# Revit family: kitchen_Sinks_Sanindusa_Belfast_With-Popup-Waste
name_source: partatom
category: Plumbing Fixtures
revit_build: Autodesk Revit 2018 (Build: 20170223_1515(x64)
units: mm (PartAtom-declared; Revit-internal decimal feet)

## family parameters
Cut with Voids When Loaded = No
Host = Face
Part Type = Normal
Room Calculation Point = No
Round Connector Dimension = Use Diameter
Shared = No

## types (1)
- kitchen_Sinks_Sanindusa_Belfast_With-Popup-Waste
    AssetType = Fixed
    CodePerformance = EN 13310:2015
    Color = white
    Constituents = Pop up waste for kitchen sink ref.4740 (included); Siphon ref. 473000 (not included)
    Default Elevation = 1219 mm
    Description = 60x46 belfast kitchen sink with pop up waste
    DrainSize = 62 mm  [stored 0.203412 ft]
    Features = "Versatile installation: topmount or undermount. Glazed on all sides except on the basis of settlement
Not rectified"
    Finish = gloss
    Installation Instructions = https://www.tec.sanindusa.pt
    Manufacturer = Sanindusa
    ManufacturerName = Sanindusa
    ManufacturerURL = www.tec.sanindusa.pt
    Material = Fine Fireclay
    Model = 740000V
    ModelNumber = 740000V
    ModelReference = Belfast
    Name = 60x46 belfast kitchen sink
    NominalHeight = 252 mm  [stored 0.826772 ft]
    NominalLength = 455 mm
    NominalWidth = 595 mm  [stored 1.9521 ft]
    ProductInformation = https://www.tec.sanindusa.pt
    ProductionYear = 2019
    Shape = rectangular
    Size = 455x595x252
    SpilloverLevel = 184
    URL = www.tec.sanindusa.pt
    WarrantyDescription = https://www.tec.sanindusa.pt
    WarrantyDurationParts = 5
    WarrantyDurationUnit = year
    Waste Connection = Yes
    Weight = 33.00 kg

note: [stored X ft] marks values corroborated as IEEE doubles in the binary element streams (Revit-internal decimal feet)

## geometry (parser evidence)
native form markers: Sweep x7
no freeform markers — native parametric forms only
